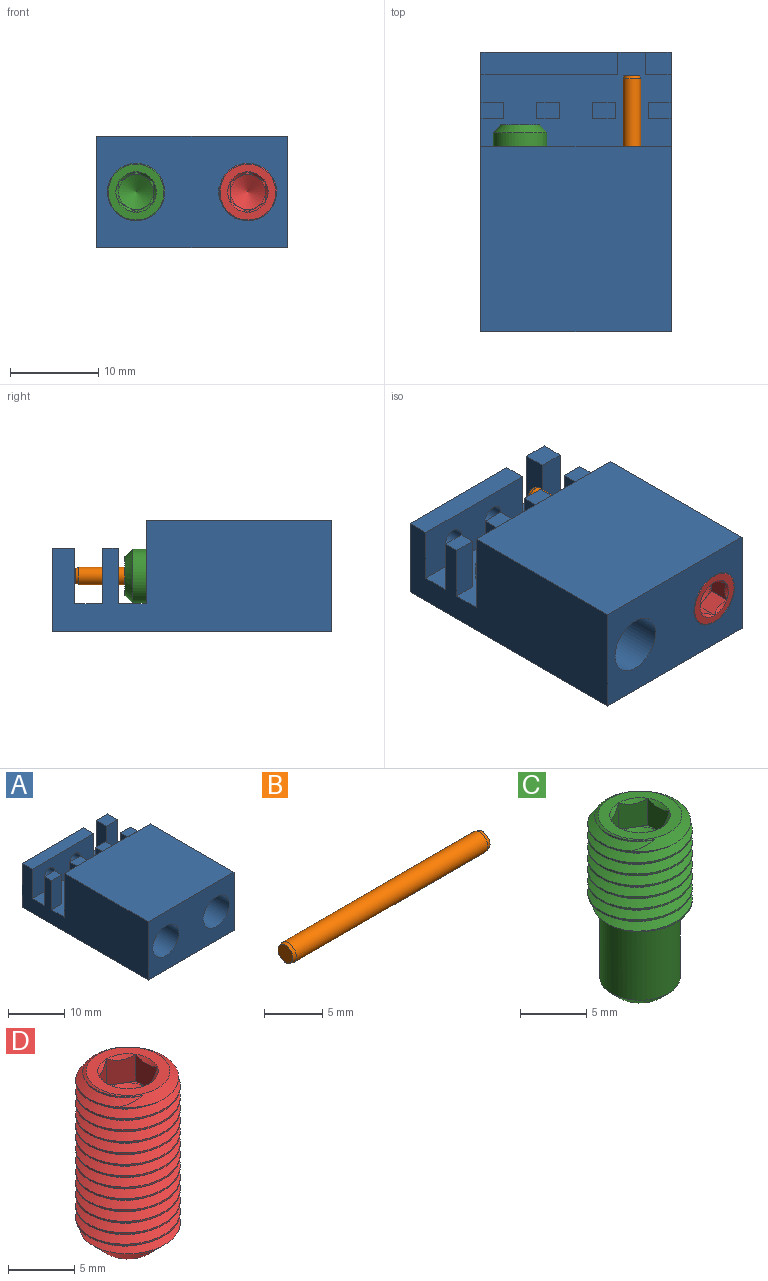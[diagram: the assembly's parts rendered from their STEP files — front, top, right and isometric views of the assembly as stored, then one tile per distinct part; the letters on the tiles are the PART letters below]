
ASSEMBLY  parts=4 mates=6
PART A: 40 faces, bbox 21.6x31.8x12.7 mm
  f0: plane 31.75x12.7mm, normal (-1,0,0), area 329mm2, adj f2,f5,f6,f7,f14,f15,f17,f18
  f1: plane 31.75x12.7mm, normal (1,0,0), area 329mm2, adj f2,f5,f6,f7,f18,f19,f21,f22
  f2: plane 21.59x9.53mm, normal (0,1,0), area 175.3mm2, adj f0,f1,f7,f23,f25,f27,f33,f35
  f3: cylinder r=1.02mm len=7.03mm, axis (0,-1,0), area 44.9mm2, adj f18,f30
  f4: cylinder r=2.54mm len=7.95mm, axis (0,-1,0), area 126.8mm2, adj f18,f28
  f5: plane 21.59x21.08mm, normal (0,0,1), area 455.2mm2, adj f0,f1,f6,f18
  f6: plane 21.59x12.7mm, normal (0,-1,0), area 207.3mm2, adj f0,f1,f5,f7,f29,f31
  f7: plane 31.75x21.59mm, normal (0,0,-1), area 685.5mm2, adj f0,f1,f2,f6
  f8: plane 6.35x1.78mm, normal (-1,0,0), area 11.3mm2, adj f9,f26,f27,f32
  f9: plane 6.35x2.54mm, normal (0,1,0), area 16.1mm2, adj f8,f10,f27,f32
  f10: plane 6.35x1.78mm, normal (1,0,0), area 11.3mm2, adj f9,f26,f27,f32
  f11: plane 6.35x1.78mm, normal (-1,0,0), area 11.3mm2, adj f12,f24,f27,f34
  f12: plane 6.35x2.54mm, normal (0,1,0), area 16.1mm2, adj f11,f13,f27,f34
  f13: plane 6.35x1.78mm, normal (1,0,0), area 11.3mm2, adj f12,f24,f27,f34
  f14: plane 15.56x6.35mm, normal (0,-1,0), area 88.7mm2, adj f0,f25,f27,f33,f38,f39
  f15: plane 6.35x2.54mm, normal (0,1,0), area 16.1mm2, adj f0,f16,f27,f37
  f16: plane 6.35x1.78mm, normal (1,0,0), area 11.3mm2, adj f15,f17,f27,f37
  f17: plane 6.35x2.54mm, normal (0,-1,0), area 16.1mm2, adj f0,f16,f27,f37
  f18: plane 21.59x9.53mm, normal (0,1,0), area 182.1mm2, adj f0,f1,f3,f4,f5,f27
  f19: plane 6.35x2.54mm, normal (0,-1,0), area 16.1mm2, adj f1,f20,f27,f36
  f20: plane 6.35x1.78mm, normal (-1,0,0), area 11.3mm2, adj f19,f21,f27,f36
  f21: plane 6.35x2.54mm, normal (0,1,0), area 16.1mm2, adj f1,f20,f27,f36
  f22: plane 6.35x2.86mm, normal (0,-1,0), area 18.1mm2, adj f1,f23,f27,f35
  f23: plane 6.35x2.54mm, normal (-1,0,0), area 16.1mm2, adj f2,f22,f27,f35
  f24: plane 6.35x2.54mm, normal (0,-1,0), area 16.1mm2, adj f11,f13,f27,f34
  f25: plane 6.35x2.54mm, normal (1,0,0), area 16.1mm2, adj f2,f14,f27,f33
  f26: plane 6.35x2.54mm, normal (0,-1,0), area 16.1mm2, adj f8,f10,f27,f32
  f27: plane 21.59x10.67mm, normal (0,0,1), area 165.5mm2, adj f0,f1,f2,f8,f9,f10,f11,f12
  f28: cone r=0mm half-angle=59deg, axis (0,-1,0), area 15.4mm2, adj f4,f29
  f29: cylinder r=3.26mm len=12.7mm, axis (0,-1,0), area 260.4mm2, adj f6,f28
  f30: cone r=0mm half-angle=59deg, axis (0,-1,0), area 35.3mm2, adj f3,f31
  f31: cylinder r=3.26mm len=12.7mm, axis (0,-1,0), area 260.4mm2, adj f6,f30
  f32: plane 2.54x1.78mm, normal (0,0,1), area 4.5mm2, adj f8,f9,f10,f26
  f33: plane 15.56x2.54mm, normal (0,0,1), area 39.5mm2, adj f0,f2,f14,f25
  f34: plane 2.54x1.78mm, normal (0,0,1), area 4.5mm2, adj f11,f12,f13,f24
  f35: plane 2.86x2.54mm, normal (0,0,1), area 7.3mm2, adj f1,f2,f22,f23
  f36: plane 2.54x1.78mm, normal (0,0,1), area 4.5mm2, adj f1,f19,f20,f21
  f37: plane 2.54x1.78mm, normal (0,0,1), area 4.5mm2, adj f0,f15,f16,f17
  f38: cylinder r=1.27mm len=2.54mm, axis (0,1,0), area 20.3mm2, adj f2,f14
  f39: cylinder r=1.27mm len=2.54mm, axis (0,1,0), area 20.3mm2, adj f2,f14
PART B: 5 faces, bbox 24x2x2 mm
  f0: cone r=1mm half-angle=15deg, axis (1,0,0), area 2.2mm2, adj f2,f4
  f1: cone r=1mm half-angle=15deg, axis (-1,0,0), area 2.2mm2, adj f2,f3
  f2: cylinder r=1mm len=23.3mm, axis (1,0,0), area 146.4mm2, adj f0,f1
  f3: plane 1.81x1.81mm, normal (1,0,0), area 2.6mm2, adj f1
  f4: plane 1.81x1.81mm, normal (-1,0,0), area 2.6mm2, adj f0
PART C: 29 faces, bbox 8.8x8.8x17.1 mm
  f0: cone r=1.98mm half-angle=60deg, axis (0,0,1), area 14.3mm2, adj f4,f5,f6,f7,f8,f18
  f1: cone r=2.29mm half-angle=45deg, axis (0,0,1), area 0.5mm2, adj f9,f23
  f2: cylinder r=3.96mm len=7.93mm, axis (0,0,1), area 23.1mm2, adj f3,f10,f12,f26
  f3: cone r=3.96mm half-angle=55deg, axis (0,0,-1), area 11.9mm2, adj f2,f9,f10,f11,f12
  f4: plane 1.72x0.99mm, normal (0,0,1), area 0.2mm2, adj f0,f23,f24
  f5: plane 1.98x0.57mm, normal (0,0,1), area 0.2mm2, adj f0,f19,f24
  f6: plane 1.72x0.99mm, normal (0,0,1), area 0.2mm2, adj f0,f19,f20
  f7: plane 1.72x0.99mm, normal (0,0,1), area 0.2mm2, adj f0,f20,f21
  f8: plane 1.98x0.57mm, normal (0,0,1), area 0.2mm2, adj f0,f21,f22
  f9: plane 7.09x7.09mm, normal (0,0,1), area 15.1mm2, adj f1,f3,f13,f14,f15,f16,f17
  f10: bspline ~8.47x7.92mm, area 130.8mm2, adj f2,f3,f11,f26
  f11: cylinder r=3.27mm len=7.91mm, axis (0,0,1), area 20.3mm2, adj f3,f10,f12,f26
  f12: bspline ~8.7x7.92mm, area 130.6mm2, adj f2,f3,f11,f26
  f13: cone r=2.29mm half-angle=45deg, axis (0,0,1), area 0mm2, adj f9,f19
  f14: cone r=2.29mm half-angle=45deg, axis (0,0,1), area 0mm2, adj f9,f20
  f15: cone r=2.29mm half-angle=45deg, axis (0,0,1), area 0mm2, adj f9,f21
  f16: cone r=2.29mm half-angle=45deg, axis (0,0,1), area 0mm2, adj f9,f22
  f17: cone r=2.29mm half-angle=45deg, axis (0,0,1), area 0mm2, adj f9,f24
  f18: plane 1.72x0.99mm, normal (0,0,1), area 0.2mm2, adj f0,f22,f23
  f19: plane 3.35x2.85mm, normal (0.5,-0.87,0), area 5.2mm2, adj f5,f6,f13,f20,f24
  f20: plane 3.35x3.16mm, normal (1,0,0), area 5.2mm2, adj f6,f7,f14,f19,f21
  f21: plane 3.35x2.85mm, normal (0.5,0.87,0), area 5.2mm2, adj f7,f8,f15,f20,f22
  f22: plane 3.35x2.85mm, normal (-0.5,0.87,0), area 5.2mm2, adj f8,f16,f18,f21,f23
  f23: plane 2.7x2.51mm, normal (-1,0,0), area 5.2mm2, adj f1,f4,f18,f22,f24
  f24: plane 3.35x2.85mm, normal (-0.5,-0.87,0), area 5.2mm2, adj f4,f5,f17,f19,f23
  f25: cylinder r=3.05mm len=7.01mm, axis (0,0,-1), area 134.3mm2, adj f26,f28
  f26: plane 7.69x7.69mm, normal (0,0,-1), area 12.1mm2, adj f2,f10,f11,f12,f25
  f27: cone r=1664.28mm half-angle=59deg, axis (0,0,-1), area 17.3mm2, adj f28
  f28: cone r=2.17mm half-angle=45deg, axis (0,0,1), area 20.3mm2, adj f25,f27
PART D: 28 faces, bbox 8.8x8.8x17.1 mm
  f0: cone r=1.98mm half-angle=60deg, axis (0,0,1), area 14.3mm2, adj f7,f8,f9,f10,f11,f21
  f1: cone r=2.29mm half-angle=45deg, axis (0,0,1), area 0.5mm2, adj f12,f26
  f2: cone r=1664.28mm half-angle=59deg, axis (0,0,-1), area 17.3mm2, adj f4
  f3: cylinder r=3.96mm len=13.53mm, axis (0,0,1), area 42.1mm2, adj f5,f6,f13,f15
  f4: cone r=2.17mm half-angle=45deg, axis (0,0,1), area 36mm2, adj f2,f5,f13,f14,f15
  f5: cone r=2.17mm half-angle=45deg, axis (0,0,1), area 1.5mm2, adj f3,f4,f13,f15
  f6: cone r=3.96mm half-angle=55deg, axis (0,0,-1), area 11.9mm2, adj f3,f12,f13,f14,f15
  f7: plane 1.72x0.99mm, normal (0,0,1), area 0.2mm2, adj f0,f26,f27
  f8: plane 1.98x0.57mm, normal (0,0,1), area 0.2mm2, adj f0,f22,f27
  f9: plane 1.72x0.99mm, normal (0,0,1), area 0.2mm2, adj f0,f22,f23
  f10: plane 1.72x0.99mm, normal (0,0,1), area 0.2mm2, adj f0,f23,f24
  f11: plane 1.98x0.57mm, normal (0,0,1), area 0.2mm2, adj f0,f24,f25
  f12: plane 7.09x7.09mm, normal (0,0,1), area 15.1mm2, adj f1,f6,f16,f17,f18,f19,f20
  f13: bspline ~15.21x7.92mm, area 240.5mm2, adj f3,f4,f5,f6,f14
  f14: cylinder r=3.27mm len=14.7mm, axis (0,0,1), area 33mm2, adj f4,f6,f13,f15
  f15: bspline ~15.21x7.92mm, area 240.2mm2, adj f3,f4,f5,f6,f14
  f16: cone r=2.29mm half-angle=45deg, axis (0,0,1), area 0mm2, adj f12,f22
  f17: cone r=2.29mm half-angle=45deg, axis (0,0,1), area 0mm2, adj f12,f23
  f18: cone r=2.29mm half-angle=45deg, axis (0,0,1), area 0mm2, adj f12,f24
  f19: cone r=2.29mm half-angle=45deg, axis (0,0,1), area 0mm2, adj f12,f25
  f20: cone r=2.29mm half-angle=45deg, axis (0,0,1), area 0mm2, adj f12,f27
  f21: plane 1.72x0.99mm, normal (0,0,1), area 0.2mm2, adj f0,f25,f26
  f22: plane 3.35x2.85mm, normal (0.5,-0.87,0), area 5.2mm2, adj f8,f9,f16,f23,f27
  f23: plane 3.35x3.16mm, normal (1,0,0), area 5.2mm2, adj f9,f10,f17,f22,f24
  f24: plane 3.35x2.85mm, normal (0.5,0.87,0), area 5.2mm2, adj f10,f11,f18,f23,f25
  f25: plane 3.35x2.85mm, normal (-0.5,0.87,0), area 5.2mm2, adj f11,f19,f21,f24,f26
  f26: plane 2.7x2.51mm, normal (-1,0,0), area 5.2mm2, adj f1,f7,f21,f25,f27
  f27: plane 3.35x2.85mm, normal (-0.5,-0.87,0), area 5.2mm2, adj f7,f8,f20,f22,f26
PLACE A at identity fixed
PLACE B rot(axis=(0.58,0.58,0.58),120deg) t=(6.35,1.21,6.35)mm
PLACE C rot(axis=(1,0,0),90deg) t=(-6.35,-0.97,6.35)mm
PLACE D rot(axis=(1,0,0),90deg) t=(6.35,-8.59,6.35)mm
MATE planar C.f27 <-> A.f39  axis (0,-1,0) through (-6.35,-8.26,6.35)mm
MATE planar D.f2 <-> A.f39  axis (0,-1,0) through (6.35,-15.88,6.35)mm
MATE cylindrical B.f0 <-> D.f2  axis (0,1,0) through (6.35,1.21,6.35)mm
MATE cylindrical C.f0 <-> A.f4  axis (0,-1,0) through (-6.35,-5.2,6.35)mm
MATE cylindrical D.f0 <-> A.f3  axis (0,-1,0) through (6.35,-12.82,6.35)mm
MATE planar B.f0 <-> D.f0  axis (0,-1,0) through (6.35,-10.79,6.35)mm
